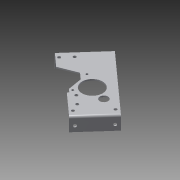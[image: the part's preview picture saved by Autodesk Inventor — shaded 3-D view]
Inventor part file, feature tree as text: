
AUTODESK INVENTOR PART (.ipt)
format: ipt  version: 2014 SP1 (Build 180222100, 222)  size: 498,176 bytes
history: native  units: in
note: dims shown in document units (in); Inventor stores cm internally (conversion verified against a paired STEP export)
features: other x24, sketch x23, sheet_metal_op x21, reference x1, extrude x1
ambient origin geometry x8: Origin, YZ Plane, XZ Plane, XY Plane, X Axis, Y Axis, Z Axis, Center Point
bodies: Body1 (feature_tree)
feature tree (70):
  sheet_metal_op  "Face2"
  sheet_metal_op  "Face5"
  sheet_metal_op  "Face6"
  sheet_metal_op  "Face7"
  sheet_metal_op  "Flange4"
  sheet_metal_op  "Flange5"
  sheet_metal_op  "Face8"
  sheet_metal_op  "Face9"
  sheet_metal_op  "Flange6"
  sheet_metal_op  "Flange7"
  sheet_metal_op  "Face13"
  sketch  "Sketch1"  dims[d8=0.125in]
  other  "Plate3"
  sketch  "Sketch8"  dims[d19=1.875in d20=0.375in d21=0.375in d22=0.375in d23=1.125in d24=1.6742in d25=1.6742in d26=1.8904in d27=0.3in d28=0.3in d29=0.3in d30=0.3in d31=0.125in]
  sketch  "Sketch9"  dims[d32=1.0in]
  other  "Plate8"
  sheet_metal_op  "Bend6"
  sketch  "Sketch10"  dims[d33=1.25in]
  sketch  "Sketch11"  dims[d86=2.0in]
  other  "Plate9"
  sheet_metal_op  "Bend7"
  sketch  "Sketch12"  dims[d87=0.125in]
  sketch  "Sketch14"  dims[d88=0.0in]
  sketch  "Sketch15"  dims[d89=3.0in]
  other  "Plate10"
  sheet_metal_op  "Bend8"
  sketch  "Sketch16"  dims[d90=0.125in]
  other  "Plate11"
  sheet_metal_op  "Bend9"
  sketch  "Sketch17"  dims[d91=0.125in]
  other  "Plate12"
  sheet_metal_op  "Bend10"
  sketch  "Sketch18"  dims[d92=0.0625in]
  sketch  "Sketch19"  dims[d93=0.25in]
  sketch  "Sketch20"  dims[d94=0.125in]
  reference  "Reference4"
  sketch  "Sketch21"  dims[d95=0.266in]
  sketch  "Sketch22"  dims[d96=0.266in]
  sketch  "Sketch23"  dims[d97=2.75in]
  other  "Plate13"
  sheet_metal_op  "Bend11"
  sketch  "Sketch24"  dims[d98=0.3125in]
  sketch  "Sketch25"  dims[d99=0.5in]
  sketch  "Sketch26"  dims[d100=0.5in]
  other  "Plate14"
  sheet_metal_op  "Bend12"
  sketch  "Sketch27"  dims[d101=0.125in]
  other  "Plate15"
  sheet_metal_op  "Bend13"
  sketch  "Sketch28"  dims[d102=0.0in]
  other  "Plate16"
  sheet_metal_op  "Bend14"
  sketch  "Sketch38"  dims[d103=3.875in]
  sketch  "Sketch39"  dims[d104=2.375in d105=0.125in d106=0.125in d107=0.0625in d108=0.25in d109=0.125in d110=0.266in d111=0.266in d112=0.5in d113=0.375in d114=1.5in d115=0.5in d116=0.125in d117=0.0in d124=0.0625in d126=0.125in d127=0.0in d128=0.2in d130=0.2in d131=0.2in d132=0.125in d133=0.125in d134=0.0625in d135=0.25in d136=0.125in d137=0.125in d138=0.0625in d139=0.25in d140=0.125in d141=1.25in d142=90.0deg d143=0.05in d144=0.5in d145=0.125in d146=0.125in d147=0.125in d148=0.0625in d149=0.25in d150=0.125in d151=1.25in d152=90.0deg d153=0.05in d154=0.5in d155=0.125in d156=0.125in d157=0.266in d158=0.266in d159=0.5in d160=0.375in d161=0.375in d162=0.5in d163=100.0in d164=0.0in d165=0.266in d166=0.375in d167=0.5in d168=0.125in d169=0.0in d171=0.748in d172=1.0in d173=24.0in d174=0.125in d175=0.0in d176=1.75in d177=0.5in d178=1.0in d179=0.266in d180=0.266in d181=0.125in d182=0.0in d183=0.2in d184=0.0687in d186=1.2992in d187=1.2992in d188=0.2in d189=0.0687in d190=1.2992in d191=1.2992in d192=0.2in d193=0.0687in d194=1.5154in d195=1.5154in d196=0.125in d197=0.0in d198=0.125in d199=0.125in d200=0.0625in d201=0.25in d202=0.125in d203=2.5in d204=0.125in d205=0.0in d206=0.25in d207=0.125in d208=0.0in d209=1.5in d210=2.25in d211=0.125in d212=0.125in d213=0.0625in d214=0.25in d215=0.125in d216=1.5in d217=0.125in d218=0.0625in d219=0.25in d220=0.125in d221=1.25in d222=90.0deg d223=0.05in d224=0.5in d225=0.125in d226=0.125in d227=0.125in d228=0.0625in d229=0.25in d230=0.125in d231=1.25in d232=90.0deg d233=0.05in d234=0.5in d235=0.125in d236=0.125in d270=90.0deg d272=0.375in d302=0.266in d303=0.266in d304=1.0in d305=0.25in d306=0.125in d307=0.0in d308=0.125in d309=0.125in d310=0.0625in d311=0.25in d312=0.125in d2=0.25in d3=0.125in d5=0.125in d6=0.0625in d7=0.25in d13=0.125in d18=1.0in]
  other  "Plate22"
  sheet_metal_op  "Bend20"
  other  "Cut2"
  other  "Cut3"
  other  "Cut4"
  other  "Cut6"
  other  "Cut7"
  other  "Cut8"
  other  "Cut9"
  other  "Cut10"
  other  "Cut12"
  other  "Cut13"
  other  "Cut18"
  other  "Cut11"
  other  "Definition1"
  extrude  "Extrusion1"  Depth=0.125in
